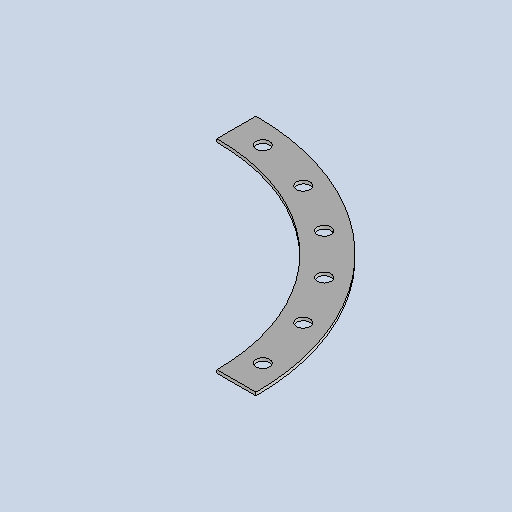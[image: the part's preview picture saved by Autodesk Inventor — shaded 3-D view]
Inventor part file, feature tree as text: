
AUTODESK INVENTOR PART (.ipt)
format: ipt  version: 2025 (Build 290162010, 162A)  size: 147,968 bytes
history: native  units: mm
features: sketch x2, other x2, sheet_metal_op x1, extrude x1, pattern_circular x1
ambient origin geometry x8: Origin, YZ Plane, XZ Plane, XY Plane, X Axis, Y Axis, Z Axis, Center Point
bodies: Solid1 (feature_tree)
feature tree (7):
  sheet_metal_op  "Face1"
  extrude  "Extrusion2"  Depth=600.0mm
  pattern_circular  "Circular Pattern1"  Count=64  [1 undecoded]
  sketch  "Sketch1"  dims[d0=502.0mm d1=600.0mm d2=640.0mm]
  other  "Plate1"
  sketch  "Sketch3"  dims[d5=4.0mm d12=550.0mm d13=1.308997mm d14=17.0mm d15=0.0mm d16=0.0mm d17=60.0mm d18=75.0deg]
  other  "Definition1"
note: 1 required parameter value undecoded (feature->parameter linkage not recoverable at this tier; creation-order binding heuristic only, values carry confidence <= 0.55)
